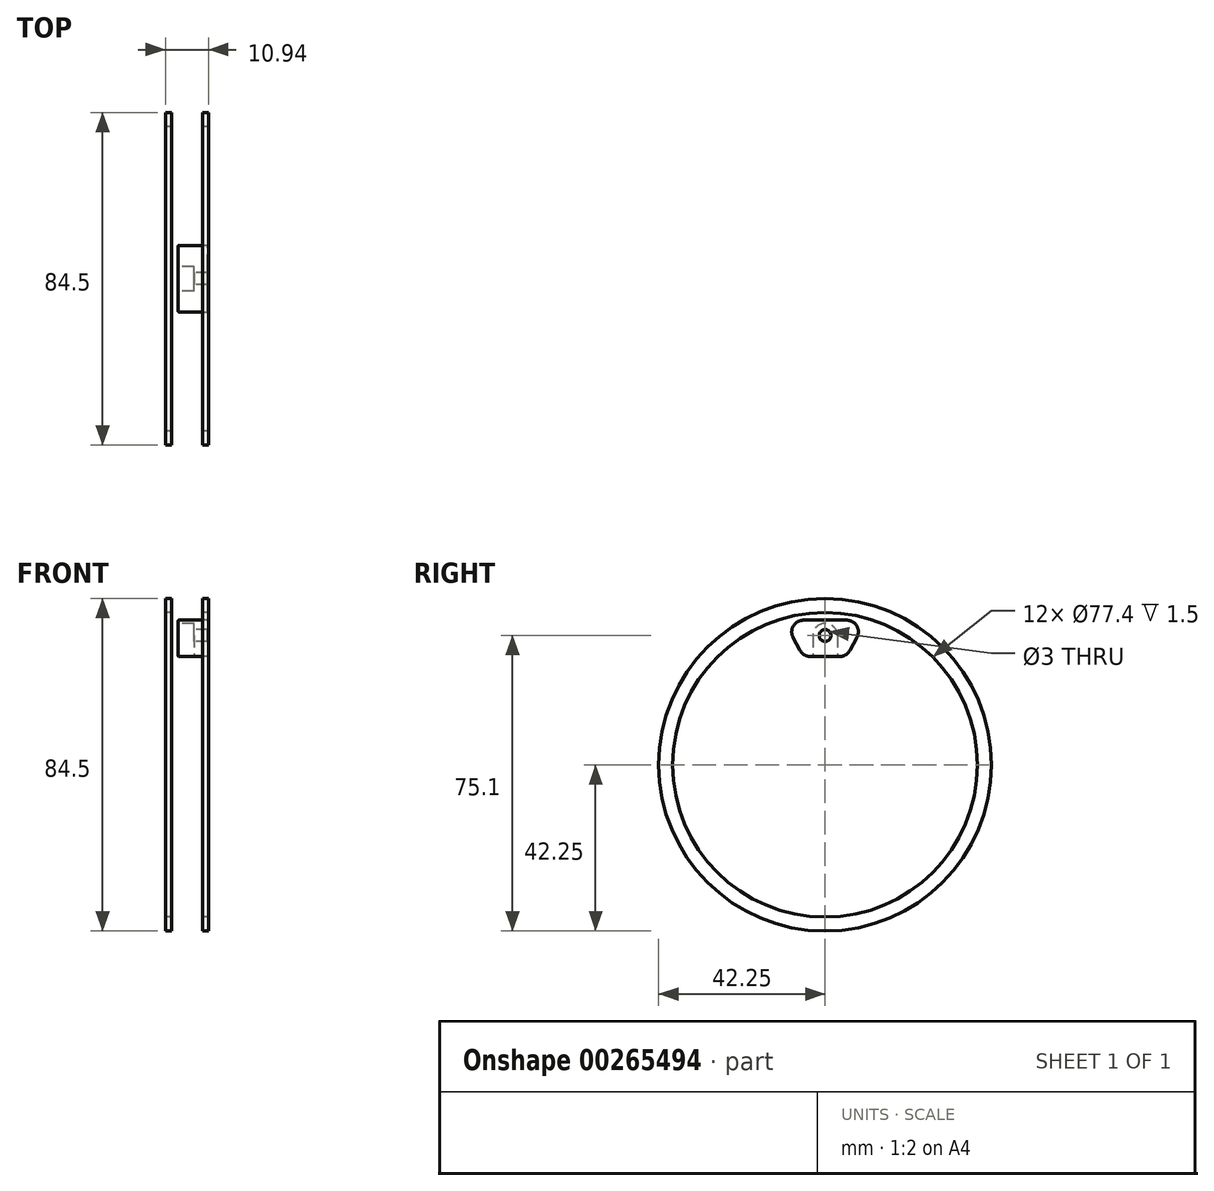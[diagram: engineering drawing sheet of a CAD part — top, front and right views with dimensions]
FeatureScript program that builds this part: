
annotation { "Feature Type Name" : "Feature", "Feature Type Description" : "" }
export const myFeature = defineFeature(function(context is Context, id is Id, definition is map)
    precondition{}
    {
        {
            var Q0;
            Q0=qCreatedBy(makeId("Front.planeOp"),FACE);
            var sketch = newSketch(context, id + "F0", { "sketchPlane" : qUnion([Q0])});
            skLineSegment(sketch, "E0", {"start": v(0, 0) * mm, "end": v(-16.32, 0) * mm, "construction": true});
            skLineSegment(sketch, "E1", {"start": v(-16.32, 0) * mm, "end": v(14.85, 0) * mm, "construction": true});
            skLineSegment(sketch, "E2", {"start": v(0, 0) * mm, "end": v(0, 42.25) * mm, "construction": true});
            skLineSegment(sketch, "E3", {"start": v(-11.67, 42.25) * mm, "end": v(-11.67, 37.25) * mm});
            skLineSegment(sketch, "E4", {"start": v(-11.66, 37.25) * mm, "end": v(-2.27, 37.15) * mm});
            skLineSegment(sketch, "E5", {"start": v(-2.27, 37.15) * mm, "end": v(-2.27, 36.75) * mm});
            skLineSegment(sketch, "E6.MirrorCS", {"start": v(11.66, 42.25) * mm, "end": v(11.66, 37.25) * mm});
            skLineSegment(sketch, "E7", {"start": v(11.67, 37.25) * mm, "end": v(4.97, 37.15) * mm});
            skLineSegment(sketch, "E8", {"start": v(4.97, 37.15) * mm, "end": v(4.97, 36.75) * mm});
            skLineSegment(sketch, "E9", {"start": v(0, 42.25) * mm, "end": v(0, 38.7) * mm, "construction": true});
            skLineSegment(sketch, "E10", {"start": v(0, 38.7) * mm, "end": v(-3.97, 38.7) * mm, "construction": true});
            skLineSegment(sketch, "E11", {"start": v(-3.97, 38.7) * mm, "end": v(-3.97, 42.25) * mm});
            skLineSegment(sketch, "E12", {"start": v(-8.67, 38.7) * mm, "end": v(-8.67, 42.25) * mm});
            skLineSegment(sketch, "E13", {"start": v(-8.67, 38.7) * mm, "end": v(-5.47, 38.7) * mm});
            skLineSegment(sketch, "E14", {"start": v(-11.67, 42.25) * mm, "end": v(-8.67, 42.25) * mm});
            skLineSegment(sketch, "E15", {"start": v(-3.97, 42.25) * mm, "end": v(-5.47, 42.25) * mm});
            skLineSegment(sketch, "E16", {"start": v(-5.47, 42.25) * mm, "end": v(-5.47, 38.7) * mm});
            skLineSegment(sketch, "E17.MirrorCS", {"start": v(11.67, 42.25) * mm, "end": v(8.67, 42.25) * mm});
            skLineSegment(sketch, "E18.MirrorCS", {"start": v(8.67, 38.7) * mm, "end": v(8.67, 42.25) * mm});
            skLineSegment(sketch, "E19.MirrorCS", {"start": v(8.67, 38.7) * mm, "end": v(5.47, 38.7) * mm});
            skLineSegment(sketch, "E20.MirrorCS", {"start": v(5.47, 42.25) * mm, "end": v(5.47, 38.7) * mm});
            skLineSegment(sketch, "E21.MirrorCS", {"start": v(3.97, 42.25) * mm, "end": v(5.47, 42.25) * mm});
            skLineSegment(sketch, "E22.MirrorCS", {"start": v(3.97, 38.7) * mm, "end": v(3.97, 42.25) * mm});
            skLineSegment(sketch, "E23", {"start": v(-3.97, 38.7) * mm, "end": v(3.97, 38.7) * mm});
            skLineSegment(sketch, "E24", {"start": v(-2.27, 36.75) * mm, "end": v(-2.27, 0) * mm, "construction": true});
            skLineSegment(sketch, "E25", {"start": v(-5.47, 38.7) * mm, "end": v(5.47, 38.7) * mm});
            skLineSegment(sketch, "E26", {"start": v(-2.27, 36.75) * mm, "end": v(4.97, 36.75) * mm});
            skSolve(sketch);
        }
        {
            var Q0;
            Q0=makeQuery(id+"F0.imprint","IMPRINT",FACE,{"disambiguationData":[TD([[makeQuery(id+"F0.imprint","IMPRINT",EDGE,{"derivedFrom":sQuery(id+"F0.wireOp",EDGE,"E3")}),1.0]])]});
            var Q1;
            {var subQ0=sQuery(id+"F0.wireOp",EDGE,"E11");Q1=makeQuery(id+"F0.imprint","IMPRINT",FACE,{"disambiguationData":[TD([[makeQuery(id+"F0.imprint","IMPRINT",EDGE,{"derivedFrom":subQ0}),1.0]])]});}
            var Q2;
            {var subQ0=sQuery(id+"F0.wireOp",EDGE,"E20.MirrorCS");Q2=makeQuery(id+"F0.imprint","IMPRINT",FACE,{"disambiguationData":[TD([[makeQuery(id+"F0.imprint","IMPRINT",EDGE,{"derivedFrom":subQ0}),-1.0]])]});}
            var Q3;
            Q3=sQuery(id+"F0.wireOp",EDGE,"E1");
            revolve(context, id + "F1", {"entities" : qUnion([Q0, Q1, Q2]), "axis" : qUnion([Q3]), "revolveType" : RevolveType.FULL});
        }
        {
            var Q0;
            Q0=makeQuery(id+"F0.imprint","IMPRINT",FACE,{"disambiguationData":[TD([[makeQuery(id+"F0.imprint","IMPRINT",EDGE,{"derivedFrom":sQuery(id+"F0.wireOp",EDGE,"E3")}),1.0]])]});
            var sketch = newSketch(context, id + "F2", { "sketchPlane" : qUnion([Q0])});
            skLineSegment(sketch, "E27", {"start": v(-2.27, 36.75) * mm, "end": v(-2.27, 27.5) * mm});
            skLineSegment(sketch, "E28", {"start": v(-2.27, 27.5) * mm, "end": v(-2.27, 0) * mm, "construction": true});
            skLineSegment(sketch, "E29.bottom", {"start": v(-2.27, 27.5) * mm, "end": v(4.97, 27.5) * mm});
            skLineSegment(sketch, "E29.top", {"start": v(-2.27, 36.75) * mm, "end": v(4.97, 36.75) * mm});
            skLineSegment(sketch, "E29.left", {"start": v(-2.27, 27.5) * mm, "end": v(-2.27, 36.75) * mm});
            skLineSegment(sketch, "E29.right", {"start": v(4.97, 27.5) * mm, "end": v(4.97, 36.75) * mm});
            skLineSegment(sketch, "E30.bottom", {"start": v(4.97, 27.5) * mm, "end": v(0.97, 27.5) * mm});
            skLineSegment(sketch, "E30.top", {"start": v(4.97, 36.75) * mm, "end": v(0.97, 36.75) * mm});
            skLineSegment(sketch, "E30.right", {"start": v(0.97, 27.5) * mm, "end": v(0.97, 36.75) * mm});
            skSolve(sketch);
        }
        {
            var Q0;
            Q0=qCreatedBy(makeId("Right.planeOp"),FACE);
            var sketch = newSketch(context, id + "F3", { "sketchPlane" : qUnion([Q0])});
            skLineSegment(sketch, "E31", {"start": v(-5.5, 27.5) * mm, "end": v(5.5, 27.5) * mm});
            skPoint(sketch, "E32.endSnap0", {"position": v(0, 36.75) * mm});
            skCircle(sketch, "E33", {"center": v(0, 32.85) * mm, "radius": 1.5 * mm});
            skLineSegment(sketch, "E34", {"start": v(0, 27.5) * mm, "end": v(0, 32.85) * mm, "construction": true});
            skCircle(sketch, "E35", {"center": v(0, 32.85) * mm, "radius": 3.1 * mm});
            skLineSegment(sketch, "E36", {"start": v(-3.1, 32.85) * mm, "end": v(-3.1, 27.5) * mm});
            skLineSegment(sketch, "E37", {"start": v(3.1, 32.85) * mm, "end": v(3.1, 27.5) * mm});
            skLineSegment(sketch, "E38", {"start": v(0, 36.75) * mm, "end": v(-10.5, 36.75) * mm});
            skLineSegment(sketch, "E39", {"start": v(-10.5, 36.75) * mm, "end": v(-5.5, 27.5) * mm});
            skLineSegment(sketch, "E40.MirrorCS", {"start": v(0, 36.75) * mm, "end": v(10.5, 36.75) * mm});
            skLineSegment(sketch, "E41.MirrorCS", {"start": v(10.5, 36.75) * mm, "end": v(5.5, 27.5) * mm});
            skSolve(sketch);
        }
        {
            var Q0;
            Q0 = qSketchRegion(id + "F3", true);
            var Q1;
            Q1=makeQuery(id+"F3.imprint","IMPRINT",FACE,{"disambiguationData":[TD([[makeQuery(id+"F3.imprint","IMPRINT",EDGE,{"derivedFrom":sQuery(id+"F3.wireOp",EDGE,"E33")}),-1.0]])]});
            var Q2;
            Q2 = qConstructionFilter(qBodyType(qCreatedBy(id + "F3" ,EDGE), BodyType.WIRE), ConstructionObject.NO);
            var Q3;
            Q3=sQuery(id+"F0.wireOp",VERTEX,"E8.end");
            extrude(context, id + "F4", {"entities" : qUnion([Q0, Q1]), "operationType" : NewBodyOperationType.ADD, "surfaceEntities" : qUnion([Q2]), "endBoundEntityVertex" : qUnion([Q3]), "depth" : 4.5 * mm, "symmetric" : true});
        }
        {
            var Q0;
            Q0=makeQuery(id+"F4.opExtrude","CAP_FACE",FACE,{"disambiguationData":[OSD([sQuery(id+"F3.wireOp",EDGE,"E31"),sQuery(id+"F3.wireOp",EDGE,"E35"),sQuery(id+"F3.wireOp",EDGE,"E38"),sQuery(id+"F3.wireOp",EDGE,"E39"),sQuery(id+"F3.wireOp",EDGE,"E40.MirrorCS"),sQuery(id+"F3.wireOp",EDGE,"E41.MirrorCS")])],"isStart":false});
            extrude(context, id + "F5", {"entities" : qUnion([Q0]), "operationType" : NewBodyOperationType.ADD, "depth" : 3 * mm});
        }
        {
            var Q0;
            Q0=makeQuery(id+"F4.opExtrude","CAP_FACE",FACE,{"disambiguationData":[OSD([sQuery(id+"F3.wireOp",EDGE,"E31"),sQuery(id+"F3.wireOp",EDGE,"E33"),sQuery(id+"F3.wireOp",EDGE,"E38"),sQuery(id+"F3.wireOp",EDGE,"E39"),sQuery(id+"F3.wireOp",EDGE,"E40.MirrorCS"),sQuery(id+"F3.wireOp",EDGE,"E41.MirrorCS")])],"isStart":true});
            var sketch = newSketch(context, id + "F6", { "sketchPlane" : qUnion([Q0])});
            skCircle(sketch, "E42", {"center": v(0, 32.85) * mm, "radius": 3.1 * mm});
            skLineSegment(sketch, "E43", {"start": v(-3.1, 32.85) * mm, "end": v(-3.1, 27.5) * mm});
            skLineSegment(sketch, "E44", {"start": v(3.1, 32.85) * mm, "end": v(3.1, 27.5) * mm});
            skLineSegment(sketch, "E45", {"start": v(-3.1, 27.5) * mm, "end": v(3.1, 27.5) * mm});
            skSolve(sketch);
        }
        {
            var Q0;
            Q0=makeQuery(id+"F6.imprint","IMPRINT",FACE,{"disambiguationData":[TD([[makeQuery(id+"F6.imprint","IMPRINT",EDGE,{"derivedFrom":makeQuery(id+"F4.opExtrude","CAP_EDGE",EDGE,{"disambiguationData":[OSD([sQuery(id+"F3.wireOp",EDGE,"E33")])],"isStart":true})}),1.0]])]});
            var Q1;
            {var subQ0=sQuery(id+"F6.wireOp",EDGE,"E43");Q1=makeQuery(id+"F6.imprint","IMPRINT",FACE,{"disambiguationData":[TD([[makeQuery(id+"F6.imprint","IMPRINT",EDGE,{"derivedFrom":subQ0}),1.0]])]});}
            extrude(context, id + "F7", {"entities" : qUnion([Q0, Q1]), "operationType" : NewBodyOperationType.REMOVE, "oppositeDirection" : true, "depth" : 4 * mm});
        }
        {
            var Q0;
            {var subQ0=sQuery(id+"F3.wireOp",EDGE,"E41.MirrorCS");var subQ1=sQuery(id+"F3.wireOp",EDGE,"E31");Q0=makeQuery(id+"F5.boolean.opBoolean","MERGE",EDGE,{"derivedFrom":[makeQuery(id+"F4.opExtrude","SWEPT_EDGE",EDGE,{"disambiguationData":[OSD([subQ1,subQ0])]}),makeQuery(id+"F5.opExtrude","SWEPT_EDGE",EDGE,{"disambiguationData":[OSD([subQ1,subQ0])]})]});}
            var Q1;
            {var subQ0=sQuery(id+"F3.wireOp",EDGE,"E39");var subQ1=sQuery(id+"F3.wireOp",EDGE,"E31");Q1=makeQuery(id+"F5.boolean.opBoolean","MERGE",EDGE,{"derivedFrom":[makeQuery(id+"F4.opExtrude","SWEPT_EDGE",EDGE,{"disambiguationData":[OSD([subQ1,subQ0])]}),makeQuery(id+"F5.opExtrude","SWEPT_EDGE",EDGE,{"disambiguationData":[OSD([subQ1,subQ0])]})]});}
            fillet(context, id + "F8", {"entities" : qUnion([Q0, Q1]), "radius" : 3 * mm, "tangentPropagation" : true, "allowEdgeOverflow" : false});
        }
        {
            var Q0;
            {var subQ0=sQuery(id+"F3.wireOp",EDGE,"E39");var subQ1=makeQuery(id+"F4.opExtrude","SWEPT_FACE",FACE,{"disambiguationData":[OSD([subQ0])]});var subQ2=sQuery(id+"F3.wireOp",EDGE,"E41.MirrorCS");var subQ3=sQuery(id+"F3.wireOp",EDGE,"E40.MirrorCS");var subQ4=sQuery(id+"F3.wireOp",EDGE,"E38");var subQ5=sQuery(id+"F3.wireOp",EDGE,"E33");var subQ6=sQuery(id+"F3.wireOp",EDGE,"E31");var subQ7=sQuery(id+"F0.wireOp",EDGE,"k0lkDJ7i-BpfG-vdbW-jxbH-Tr7NAzdU2sUH");var subQ8=makeQuery(id+"F1.opRevolve","SWEPT_FACE",FACE,{"disambiguationData":[OSD([subQ7])]});Q0=makeQuery(id+"F5.boolean.opBoolean","MERGE",EDGE,{"derivedFrom":[makeQuery(id+"F4.boolean.opBoolean","INTERSECT",EDGE,{"derivedFrom":[subQ8,subQ1]}),makeQuery(id+"F5.opExtrude","SWEPT_EDGE",EDGE,{"disambiguationData":[OSD([subQ7,subQ6,subQ5,subQ4,subQ0,subQ3,subQ2]),TDD([makeQuery(id+"F4.boolean.opBoolean","INTERSECT",VERTEX,{"derivedFrom":[subQ8,makeQuery(id+"F4.opExtrude","CAP_FACE",FACE,{"disambiguationData":[OSD([subQ6,subQ5,subQ4,subQ0,subQ3,subQ2])],"isStart":false}),subQ1]})])]})]});}
            var Q1;
            {var subQ0=sQuery(id+"F3.wireOp",EDGE,"E41.MirrorCS");var subQ1=makeQuery(id+"F4.opExtrude","SWEPT_FACE",FACE,{"disambiguationData":[OSD([subQ0])]});var subQ2=sQuery(id+"F3.wireOp",EDGE,"E40.MirrorCS");var subQ3=sQuery(id+"F3.wireOp",EDGE,"E39");var subQ4=sQuery(id+"F3.wireOp",EDGE,"E38");var subQ5=sQuery(id+"F3.wireOp",EDGE,"E33");var subQ6=sQuery(id+"F3.wireOp",EDGE,"E31");var subQ7=sQuery(id+"F0.wireOp",EDGE,"k0lkDJ7i-BpfG-vdbW-jxbH-Tr7NAzdU2sUH");var subQ8=makeQuery(id+"F1.opRevolve","SWEPT_FACE",FACE,{"disambiguationData":[OSD([subQ7])]});Q1=makeQuery(id+"F5.boolean.opBoolean","MERGE",EDGE,{"derivedFrom":[makeQuery(id+"F4.boolean.opBoolean","INTERSECT",EDGE,{"derivedFrom":[subQ8,subQ1]}),makeQuery(id+"F5.opExtrude","SWEPT_EDGE",EDGE,{"disambiguationData":[OSD([subQ7,subQ6,subQ5,subQ4,subQ3,subQ2,subQ0]),TDD([makeQuery(id+"F4.boolean.opBoolean","INTERSECT",VERTEX,{"derivedFrom":[subQ8,makeQuery(id+"F4.opExtrude","CAP_FACE",FACE,{"disambiguationData":[OSD([subQ6,subQ5,subQ4,subQ3,subQ2,subQ0])],"isStart":false}),subQ1]})])]})]});}
            fillet(context, id + "F9", {"entities" : qUnion([Q0, Q1]), "radius" : 3 * mm, "tangentPropagation" : true, "allowEdgeOverflow" : false});
        }
        {
            var Q0;
            {var subQ0=sQuery(id+"F3.wireOp",EDGE,"E41.MirrorCS");var subQ1=sQuery(id+"F3.wireOp",EDGE,"E40.MirrorCS");var subQ2=sQuery(id+"F3.wireOp",EDGE,"E39");var subQ3=sQuery(id+"F3.wireOp",EDGE,"E38");var subQ4=sQuery(id+"F3.wireOp",EDGE,"E33");var subQ5=sQuery(id+"F3.wireOp",EDGE,"E31");var subQ6=makeQuery(id+"F4.opExtrude","SWEPT_FACE",FACE,{"disambiguationData":[OSD([subQ0])]});var subQ7=sQuery(id+"F0.wireOp",EDGE,"k0lkDJ7i-BpfG-vdbW-jxbH-Tr7NAzdU2sUH");var subQ8=makeQuery(id+"F1.opRevolve","SWEPT_FACE",FACE,{"disambiguationData":[OSD([subQ7])]});Q0=makeQuery(id+"F9.opFillet","BLEND_EDGE",EDGE,{"blendedFrom":[makeQuery(id+"F5.boolean.opBoolean","MERGE",EDGE,{"derivedFrom":[makeQuery(id+"F4.boolean.opBoolean","INTERSECT",EDGE,{"derivedFrom":[subQ8,subQ6]}),makeQuery(id+"F5.opExtrude","SWEPT_EDGE",EDGE,{"disambiguationData":[OSD([subQ7,subQ5,subQ4,subQ3,subQ2,subQ1,subQ0]),TDD([makeQuery(id+"F4.boolean.opBoolean","INTERSECT",VERTEX,{"derivedFrom":[subQ8,makeQuery(id+"F4.opExtrude","CAP_FACE",FACE,{"disambiguationData":[OSD([subQ5,subQ4,subQ3,subQ2,subQ1,subQ0])],"isStart":false}),subQ6]})])]})]}),makeQuery(id+"F4.opExtrude","CAP_FACE",FACE,{"disambiguationData":[OSD([subQ5,subQ4,subQ3,subQ2,subQ1,subQ0])],"isStart":true})],"blendedInto":[makeQuery(id+"F4.opExtrude","CAP_FACE",FACE,{"disambiguationData":[OSD([subQ5,subQ4,subQ3,subQ2,subQ1,subQ0])],"isStart":true})]});}
            var Q1;
            {var subQ0=sQuery(id+"F3.wireOp",EDGE,"E41.MirrorCS");var subQ1=makeQuery(id+"F4.opExtrude","SWEPT_FACE",FACE,{"disambiguationData":[OSD([subQ0])]});var subQ2=sQuery(id+"F3.wireOp",EDGE,"E40.MirrorCS");var subQ3=sQuery(id+"F3.wireOp",EDGE,"E39");var subQ4=sQuery(id+"F3.wireOp",EDGE,"E38");var subQ5=sQuery(id+"F3.wireOp",EDGE,"E33");var subQ6=sQuery(id+"F3.wireOp",EDGE,"E31");var subQ7=sQuery(id+"F0.wireOp",EDGE,"k0lkDJ7i-BpfG-vdbW-jxbH-Tr7NAzdU2sUH");var subQ8=makeQuery(id+"F1.opRevolve","SWEPT_FACE",FACE,{"disambiguationData":[OSD([subQ7])]});Q1=makeQuery(id+"F9.opFillet","BLEND_EDGE",EDGE,{"blendedFrom":[makeQuery(id+"F5.boolean.opBoolean","MERGE",EDGE,{"derivedFrom":[makeQuery(id+"F4.boolean.opBoolean","INTERSECT",EDGE,{"derivedFrom":[subQ8,subQ1]}),makeQuery(id+"F5.opExtrude","SWEPT_EDGE",EDGE,{"disambiguationData":[OSD([subQ7,subQ6,subQ5,subQ4,subQ3,subQ2,subQ0]),TDD([makeQuery(id+"F4.boolean.opBoolean","INTERSECT",VERTEX,{"derivedFrom":[subQ8,makeQuery(id+"F4.opExtrude","CAP_FACE",FACE,{"disambiguationData":[OSD([subQ6,subQ5,subQ4,subQ3,subQ2,subQ0])],"isStart":false}),subQ1]})])]})]}),makeQuery(id+"F1.opRevolve","SWEPT_FACE",FACE,{"disambiguationData":[OSD([sQuery(id+"F0.wireOp",EDGE,"E8")])]})],"blendedInto":[makeQuery(id+"F1.opRevolve","SWEPT_FACE",FACE,{"disambiguationData":[OSD([sQuery(id+"F0.wireOp",EDGE,"E8")])]})]});}
            var Q2;
            Q2=makeQuery(id+"F7.boolean.opBoolean","COPY",EDGE,{"derivedFrom":makeQuery(id+"F7.opExtrude","CAP_EDGE",EDGE,{"disambiguationData":[OSD([sQuery(id+"F6.wireOp",EDGE,"E43")])],"isStart":true})});
            var Q3;
            {var subQ0=sQuery(id+"F3.wireOp",EDGE,"E39");var subQ1=sQuery(id+"F3.wireOp",EDGE,"E31");Q3=makeQuery(id+"F8.opFillet","BLEND_EDGE",EDGE,{"blendedFrom":[makeQuery(id+"F5.boolean.opBoolean","MERGE",EDGE,{"derivedFrom":[makeQuery(id+"F4.opExtrude","SWEPT_EDGE",EDGE,{"disambiguationData":[OSD([subQ1,subQ0])]}),makeQuery(id+"F5.opExtrude","SWEPT_EDGE",EDGE,{"disambiguationData":[OSD([subQ1,subQ0])]})]}),makeQuery(id+"F4.opExtrude","CAP_FACE",FACE,{"disambiguationData":[OSD([subQ1,sQuery(id+"F3.wireOp",EDGE,"E33"),sQuery(id+"F3.wireOp",EDGE,"E38"),subQ0,sQuery(id+"F3.wireOp",EDGE,"E40.MirrorCS"),sQuery(id+"F3.wireOp",EDGE,"E41.MirrorCS")])],"isStart":true})],"blendedInto":[makeQuery(id+"F4.opExtrude","CAP_FACE",FACE,{"disambiguationData":[OSD([subQ1,sQuery(id+"F3.wireOp",EDGE,"E33"),sQuery(id+"F3.wireOp",EDGE,"E38"),subQ0,sQuery(id+"F3.wireOp",EDGE,"E40.MirrorCS"),sQuery(id+"F3.wireOp",EDGE,"E41.MirrorCS")])],"isStart":true})]});}
            var Q4;
            {var subQ0=sQuery(id+"F3.wireOp",EDGE,"E39");var subQ1=makeQuery(id+"F4.opExtrude","SWEPT_FACE",FACE,{"disambiguationData":[OSD([subQ0])]});var subQ2=sQuery(id+"F3.wireOp",EDGE,"E41.MirrorCS");var subQ3=sQuery(id+"F3.wireOp",EDGE,"E40.MirrorCS");var subQ4=sQuery(id+"F3.wireOp",EDGE,"E38");var subQ5=sQuery(id+"F3.wireOp",EDGE,"E33");var subQ6=sQuery(id+"F3.wireOp",EDGE,"E31");var subQ7=sQuery(id+"F0.wireOp",EDGE,"k0lkDJ7i-BpfG-vdbW-jxbH-Tr7NAzdU2sUH");var subQ8=makeQuery(id+"F1.opRevolve","SWEPT_FACE",FACE,{"disambiguationData":[OSD([subQ7])]});Q4=makeQuery(id+"F9.opFillet","BLEND_EDGE",EDGE,{"blendedFrom":[makeQuery(id+"F5.boolean.opBoolean","MERGE",EDGE,{"derivedFrom":[makeQuery(id+"F4.boolean.opBoolean","INTERSECT",EDGE,{"derivedFrom":[subQ8,subQ1]}),makeQuery(id+"F5.opExtrude","SWEPT_EDGE",EDGE,{"disambiguationData":[OSD([subQ7,subQ6,subQ5,subQ4,subQ0,subQ3,subQ2]),TDD([makeQuery(id+"F4.boolean.opBoolean","INTERSECT",VERTEX,{"derivedFrom":[subQ8,makeQuery(id+"F4.opExtrude","CAP_FACE",FACE,{"disambiguationData":[OSD([subQ6,subQ5,subQ4,subQ0,subQ3,subQ2])],"isStart":false}),subQ1]})])]})]}),makeQuery(id+"F1.opRevolve","SWEPT_FACE",FACE,{"disambiguationData":[OSD([sQuery(id+"F0.wireOp",EDGE,"E8")])]})],"blendedInto":[makeQuery(id+"F1.opRevolve","SWEPT_FACE",FACE,{"disambiguationData":[OSD([sQuery(id+"F0.wireOp",EDGE,"E8")])]})]});}
            var Q5;
            {var subQ0=sQuery(id+"F3.wireOp",EDGE,"E39");var subQ1=sQuery(id+"F3.wireOp",EDGE,"E31");Q5=makeQuery(id+"F8.opFillet","BLEND_EDGE",EDGE,{"blendedFrom":[makeQuery(id+"F5.boolean.opBoolean","MERGE",EDGE,{"derivedFrom":[makeQuery(id+"F4.opExtrude","SWEPT_EDGE",EDGE,{"disambiguationData":[OSD([subQ1,subQ0])]}),makeQuery(id+"F5.opExtrude","SWEPT_EDGE",EDGE,{"disambiguationData":[OSD([subQ1,subQ0])]})]}),makeQuery(id+"F5.opExtrude","CAP_FACE",FACE,{"disambiguationData":[OSD([subQ1,sQuery(id+"F3.wireOp",EDGE,"E33"),sQuery(id+"F3.wireOp",EDGE,"E38"),subQ0,sQuery(id+"F3.wireOp",EDGE,"E40.MirrorCS"),sQuery(id+"F3.wireOp",EDGE,"E41.MirrorCS")])],"isStart":false})],"blendedInto":[makeQuery(id+"F5.opExtrude","CAP_FACE",FACE,{"disambiguationData":[OSD([subQ1,sQuery(id+"F3.wireOp",EDGE,"E33"),sQuery(id+"F3.wireOp",EDGE,"E38"),subQ0,sQuery(id+"F3.wireOp",EDGE,"E40.MirrorCS"),sQuery(id+"F3.wireOp",EDGE,"E41.MirrorCS")])],"isStart":false})]});}
            var Q6;
            Q6=makeQuery(id+"F7.boolean.opBoolean","COPY",EDGE,{"derivedFrom":makeQuery(id+"F7.opExtrude","CAP_EDGE",EDGE,{"disambiguationData":[OSD([sQuery(id+"F6.wireOp",EDGE,"E45")])],"isStart":false})});
            var Q7;
            Q7=makeQuery(id+"F7.boolean.opBoolean","COPY",EDGE,{"derivedFrom":makeQuery(id+"F7.opExtrude","SWEPT_EDGE",EDGE,{"disambiguationData":[OSD([sQuery(id+"F3.wireOp",EDGE,"E31"),sQuery(id+"F6.wireOp",EDGE,"E43"),sQuery(id+"F6.wireOp",EDGE,"E45")])]})});
            var Q8;
            Q8=makeQuery(id+"F7.boolean.opBoolean","COPY",EDGE,{"derivedFrom":makeQuery(id+"F7.opExtrude","SWEPT_EDGE",EDGE,{"disambiguationData":[OSD([sQuery(id+"F3.wireOp",EDGE,"E31"),sQuery(id+"F6.wireOp",EDGE,"E44"),sQuery(id+"F6.wireOp",EDGE,"E45")])]})});
            fillet(context, id + "F10", {"entities" : qUnion([Q0, Q1, Q2, Q3, Q4, Q5, Q6, Q7, Q8]), "radius" : 0.2 * mm, "tangentPropagation" : true, "allowEdgeOverflow" : false});
        }
        {
            var Q0;
            Q0=makeQuery(id+"F1.opRevolve","SWEPT_BODY",BODY,{"disambiguationData":[OSD([sQuery(id+"F0.wireOp",EDGE,"E3"),sQuery(id+"F0.wireOp",EDGE,"E4"),sQuery(id+"F0.wireOp",EDGE,"E5"),sQuery(id+"F0.wireOp",EDGE,"E6.MirrorCS"),sQuery(id+"F0.wireOp",EDGE,"E7"),sQuery(id+"F0.wireOp",EDGE,"E8"),sQuery(id+"F0.wireOp",EDGE,"k0lkDJ7i-BpfG-vdbW-jxbH-Tr7NAzdU2sUH"),sQuery(id+"F0.wireOp",EDGE,"E11"),sQuery(id+"F0.wireOp",EDGE,"E12"),sQuery(id+"F0.wireOp",EDGE,"E13"),sQuery(id+"F0.wireOp",EDGE,"B3TP8W6g-5Vhm-3hPd-ryCb-lsEigtgUvEEY"),sQuery(id+"F0.wireOp",EDGE,"E14"),sQuery(id+"F0.wireOp",EDGE,"c90OOuqq-MhDp-A3KU-goeR-znRhfskGeAlH"),sQuery(id+"F0.wireOp",EDGE,"ndzZSOmN-fFcR-fRX2-1Zjp-ti7Mh20vMfT9"),sQuery(id+"F0.wireOp",EDGE,"E15"),sQuery(id+"F0.wireOp",EDGE,"E16"),sQuery(id+"F0.wireOp",EDGE,"0jZ2BNiJ-Da5U-Dujx-AnAY-nmmlqta5gxTO"),sQuery(id+"F0.wireOp",EDGE,"E17.MirrorCS"),sQuery(id+"F0.wireOp",EDGE,"E18.MirrorCS"),sQuery(id+"F0.wireOp",EDGE,"E19.MirrorCS"),sQuery(id+"F0.wireOp",EDGE,"0e83bd74-4e9d-4adb-ac6d-f1e305203bed0.MirrorCS"),sQuery(id+"F0.wireOp",EDGE,"3e0bd0f0-6244-494c-92e2-7133a7591ea60.MirrorCS"),sQuery(id+"F0.wireOp",EDGE,"1eda7761-fbfe-4b35-8e03-3b719253ca290.MirrorCS"),sQuery(id+"F0.wireOp",EDGE,"550b1c4a-01cb-477d-b5ec-ad1d9ec0e4bc0.MirrorCS"),sQuery(id+"F0.wireOp",EDGE,"E20.MirrorCS"),sQuery(id+"F0.wireOp",EDGE,"E21.MirrorCS"),sQuery(id+"F0.wireOp",EDGE,"E22.MirrorCS"),sQuery(id+"F0.wireOp",EDGE,"E23")])]});
            var Q1;
            Q1=sQuery(id+"F0.wireOp",EDGE,"E1");
            circularPattern(context, id + "F11", {"operationType" : NewBodyOperationType.ADD, "entities" : qUnion([Q0]), "axis" : qUnion([Q1]), "angle" : 360 * degree, "instanceCount" : 6, "equalSpace" : true});
        }
    });
